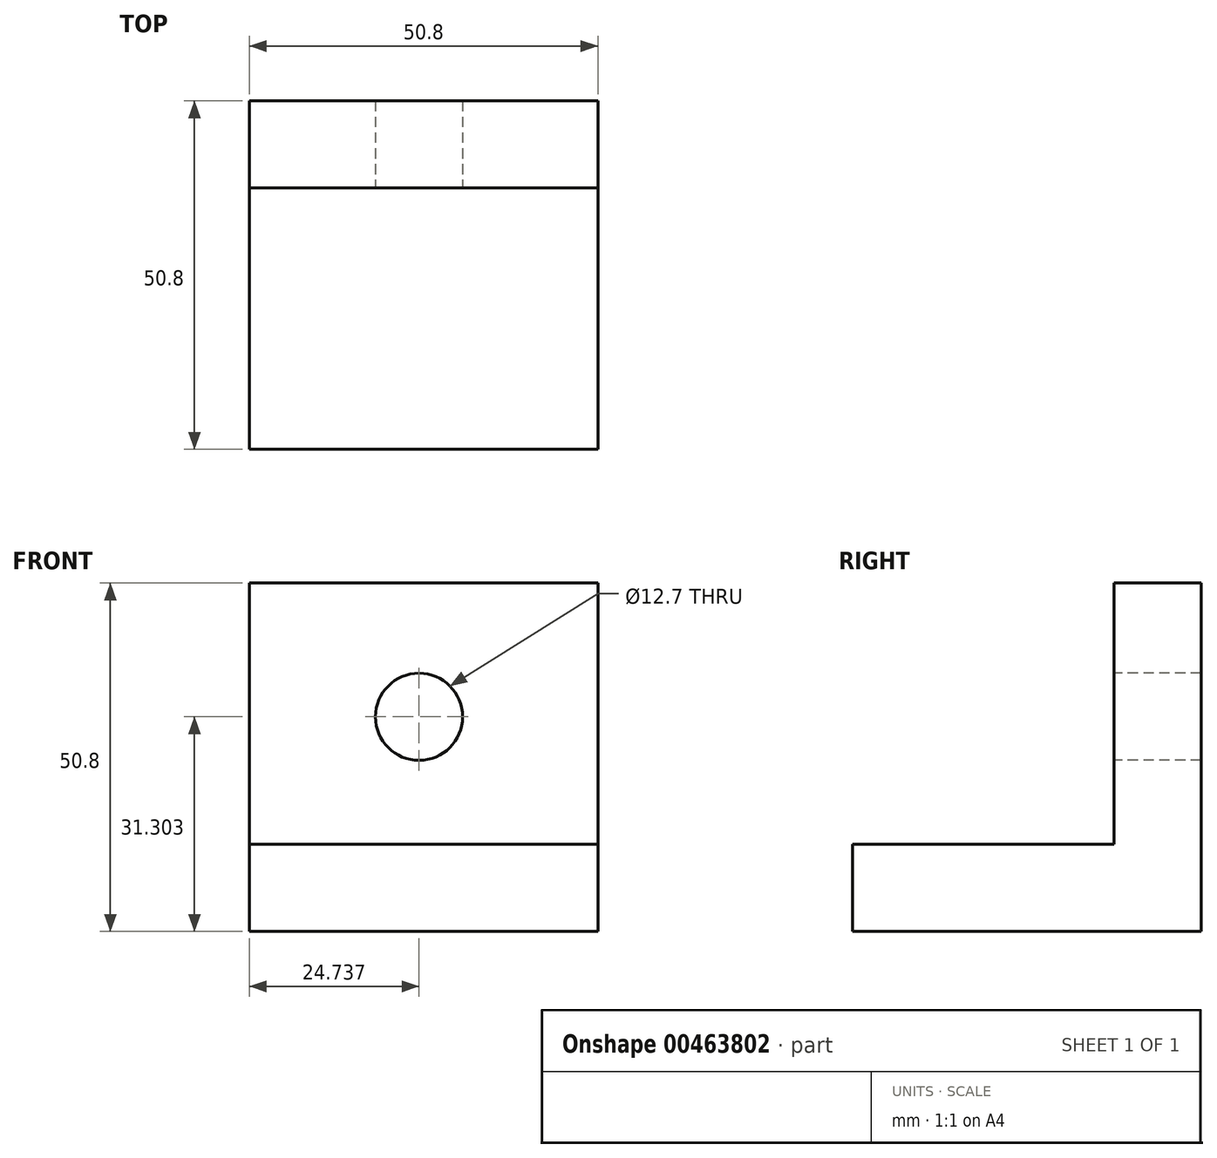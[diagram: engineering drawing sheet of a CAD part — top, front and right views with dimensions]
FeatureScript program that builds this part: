
annotation { "Feature Type Name" : "Feature", "Feature Type Description" : "" }
export const myFeature = defineFeature(function(context is Context, id is Id, definition is map)
    precondition{}
    {
        {
            var Q0;
            Q0=qCreatedBy(makeId("Top.planeOp"),FACE);
            var sketch = newSketch(context, id + "F0", { "sketchPlane" : qUnion([Q0])});
            skLineSegment(sketch, "E0", {"start": v(-36.73, 53.79) * mm, "end": v(-36.73, 2.99) * mm});
            skLineSegment(sketch, "E1", {"start": v(-36.73, 2.99) * mm, "end": v(14.07, 2.99) * mm});
            skLineSegment(sketch, "E2", {"start": v(14.07, 2.99) * mm, "end": v(14.07, 53.79) * mm});
            skLineSegment(sketch, "E3", {"start": v(14.07, 53.79) * mm, "end": v(-36.73, 53.79) * mm});
            skSolve(sketch);
        }
        {
            var Q0;
            Q0 = qSketchRegion(id + "F0", true);
            extrude(context, id + "F1", {"entities" : qUnion([Q0]), "depth" : 12.7 * mm});
        }
        {
            var Q0;
            Q0=makeQuery(id+"F1.opExtrude","CAP_FACE",FACE,{"disambiguationData":[OSD([sQuery(id+"F0.wireOp",EDGE,"E0"),sQuery(id+"F0.wireOp",EDGE,"E1"),sQuery(id+"F0.wireOp",EDGE,"E2"),sQuery(id+"F0.wireOp",EDGE,"E3")])],"isStart":false});
            var sketch = newSketch(context, id + "F2", { "sketchPlane" : qUnion([Q0])});
            skLineSegment(sketch, "E4", {"start": v(-36.73, 53.79) * mm, "end": v(14.07, 53.79) * mm});
            skLineSegment(sketch, "E5", {"start": v(14.07, 53.79) * mm, "end": v(14.07, 41.09) * mm});
            skLineSegment(sketch, "E6", {"start": v(14.07, 41.09) * mm, "end": v(-36.73, 41.09) * mm});
            skLineSegment(sketch, "E7", {"start": v(-36.73, 41.09) * mm, "end": v(-36.73, 53.79) * mm});
            skSolve(sketch);
        }
        {
            var Q0;
            Q0 = qSketchRegion(id + "F2", true);
            extrude(context, id + "F3", {"entities" : qUnion([Q0]), "operationType" : NewBodyOperationType.ADD, "depth" : 38.1 * mm});
        }
        {
            var Q0;
            Q0=makeQuery(id+"F3.opExtrude","SWEPT_FACE",FACE,{"disambiguationData":[OSD([sQuery(id+"F2.wireOp",EDGE,"E6")])]});
            var sketch = newSketch(context, id + "F4", { "sketchPlane" : qUnion([Q0])});
            skCircle(sketch, "E8", {"center": v(-12, 31.3) * mm, "radius": 6.35 * mm});
            skSolve(sketch);
        }
        {
            var Q0;
            Q0=makeQuery(id+"F4.imprint","IMPRINT",FACE,{"disambiguationData":[TD([[makeQuery(id+"F4.imprint","IMPRINT",EDGE,{"derivedFrom":sQuery(id+"F4.wireOp",EDGE,"E8")}),1.0]])]});
            extrude(context, id + "F5", {"entities" : qUnion([Q0]), "operationType" : NewBodyOperationType.REMOVE, "oppositeDirection" : true, "depth" : 25.4 * mm});
        }
    });
